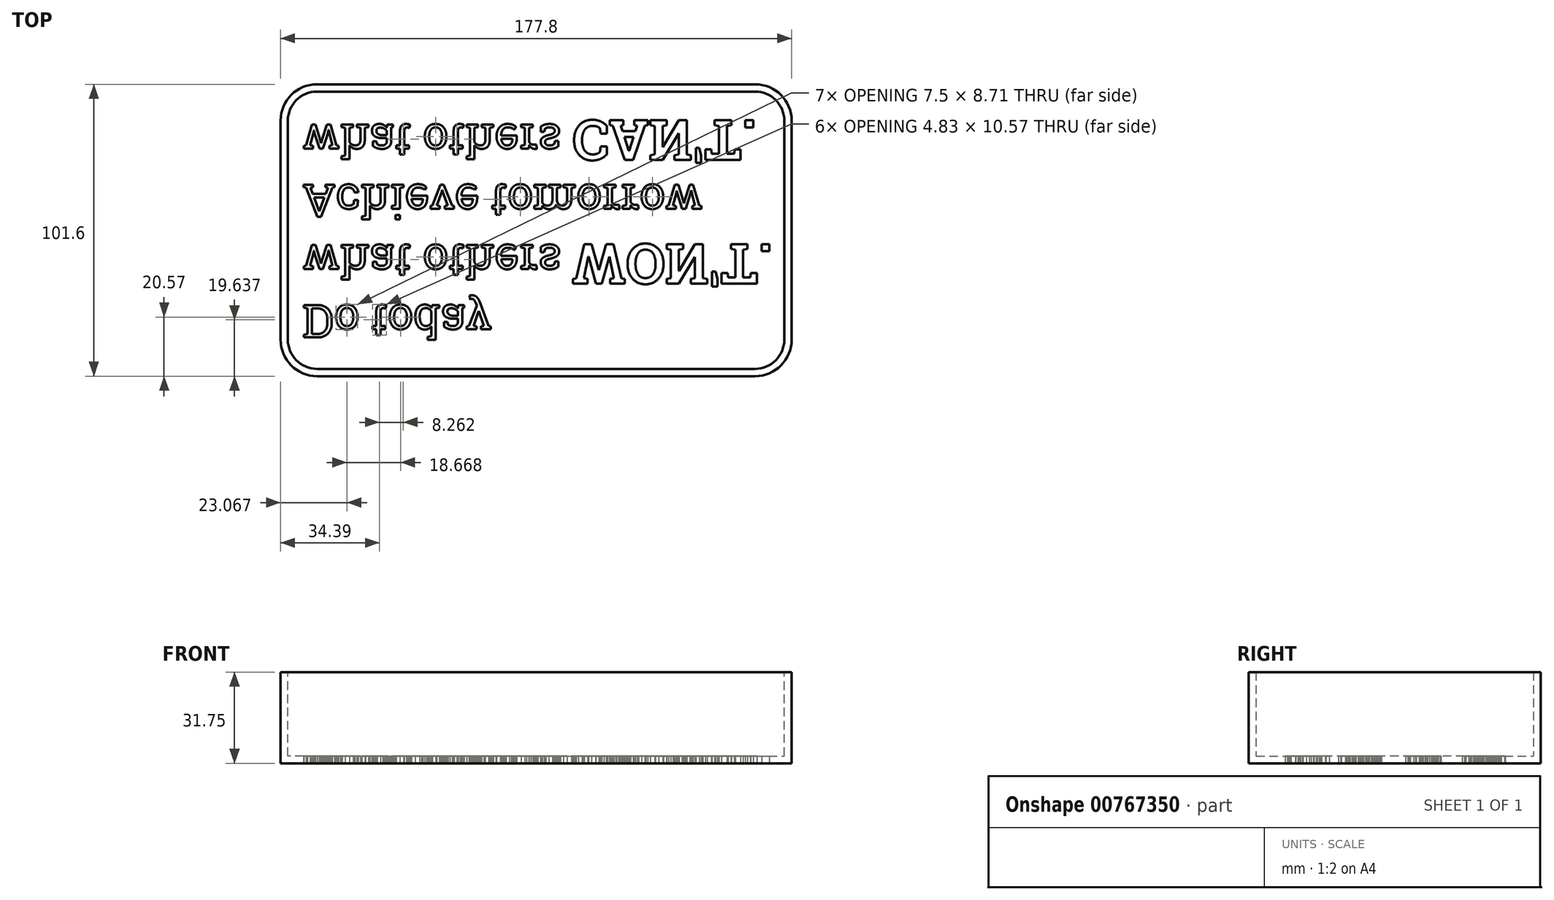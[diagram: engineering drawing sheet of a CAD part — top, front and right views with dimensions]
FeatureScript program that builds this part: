
annotation { "Feature Type Name" : "Feature", "Feature Type Description" : "" }
export const myFeature = defineFeature(function(context is Context, id is Id, definition is map)
    precondition{}
    {
        {
            var Q0;
            Q0=qCreatedBy(makeId("Top.planeOp"),FACE);
            var sketch = newSketch(context, id + "F0", { "sketchPlane" : qUnion([Q0])});
            skLineSegment(sketch, "E0.bottom", {"start": v(-88.9, 50.8) * mm, "end": v(88.9, 50.8) * mm});
            skLineSegment(sketch, "E0.top", {"start": v(-88.9, -50.8) * mm, "end": v(88.9, -50.8) * mm});
            skLineSegment(sketch, "E0.left", {"start": v(-88.9, 50.8) * mm, "end": v(-88.9, -50.8) * mm});
            skLineSegment(sketch, "E0.right", {"start": v(88.9, 50.8) * mm, "end": v(88.9, -50.8) * mm});
            skPoint(sketch, "E0.middle", {"position": v(0, 0) * mm});
            skSolve(sketch);
        }
        {
            var Q0;
            Q0 = qSketchRegion(id + "F0", true);
            extrude(context, id + "F1", {"entities" : qUnion([Q0]), "oppositeDirection" : true, "depth" : 31.75 * mm, "offsetDistance" : 25.4 * mm});
        }
        {
            var Q0;
            Q0=makeQuery(id+"F1.opExtrude","SWEPT_EDGE",EDGE,{"disambiguationData":[OSD([sQuery(id+"F0.wireOp",EDGE,"E0.bottom"),sQuery(id+"F0.wireOp",EDGE,"E0.right")])]});
            var Q1;
            Q1=makeQuery(id+"F1.opExtrude","SWEPT_EDGE",EDGE,{"disambiguationData":[OSD([sQuery(id+"F0.wireOp",EDGE,"E0.bottom"),sQuery(id+"F0.wireOp",EDGE,"E0.left")])]});
            var Q2;
            Q2=makeQuery(id+"F1.opExtrude","SWEPT_EDGE",EDGE,{"disambiguationData":[OSD([sQuery(id+"F0.wireOp",EDGE,"E0.top"),sQuery(id+"F0.wireOp",EDGE,"E0.right")])]});
            var Q3;
            Q3=makeQuery(id+"F1.opExtrude","SWEPT_EDGE",EDGE,{"disambiguationData":[OSD([sQuery(id+"F0.wireOp",EDGE,"E0.top"),sQuery(id+"F0.wireOp",EDGE,"E0.left")])]});
            fillet(context, id + "F2", {"entities" : qUnion([Q0, Q1, Q2, Q3]), "radius" : 12.7 * mm, "tangentPropagation" : true, "allowEdgeOverflow" : false});
        }
        {
            var Q0;
            Q0=makeQuery(id+"F1.opExtrude","CAP_FACE",FACE,{"disambiguationData":[OSD([sQuery(id+"F0.wireOp",EDGE,"E0.bottom"),sQuery(id+"F0.wireOp",EDGE,"E0.top"),sQuery(id+"F0.wireOp",EDGE,"E0.left"),sQuery(id+"F0.wireOp",EDGE,"E0.right")])],"isStart":true});
            shell(context, id + "F3", {"entities" : qUnion([Q0]), "thickness" : 2.54 * mm});
        }
        {
            var Q0;
            Q0=makeQuery(id+"F1.opExtrude","CAP_FACE",FACE,{"disambiguationData":[OSD([sQuery(id+"F0.wireOp",EDGE,"E0.bottom"),sQuery(id+"F0.wireOp",EDGE,"E0.top"),sQuery(id+"F0.wireOp",EDGE,"E0.left"),sQuery(id+"F0.wireOp",EDGE,"E0.right")])],"isStart":false});
            var sketch = newSketch(context, id + "F4", { "sketchPlane" : qUnion([Q0])});
            skText(sketch, "E1", { "text": "Do today \nwhat others \nAchieve tomorrow \nwhat others ", "fontName": "RobotoSlab-Regular.ttf"});
            skText(sketch, "E2", { "text": "WON\'T.", "fontName": "RobotoSlab-Bold.ttf"});
            skText(sketch, "E3", { "text": "CAN\'T.", "fontName": "RobotoSlab-Bold.ttf"});
            const initialGuessF4  = {"E1": [-0.08128, 0.02604, 1, 0, 0.01143], "E2": [0.0125, 0.00483, 1, 0, 0.01397], "E3": [0.01274, -0.03824, 1, 0, 0.01397]};
            skSetInitialGuess(sketch, initialGuessF4);
            skSolve(sketch);
        }
        {
            var Q0;
            Q0 = qSketchRegion(id + "F4", true);
            extrude(context, id + "F5", {"entities" : qUnion([Q0]), "operationType" : NewBodyOperationType.REMOVE, "oppositeDirection" : true, "depth" : 25.4 * mm, "offsetDistance" : 25.4 * mm});
        }
    });
